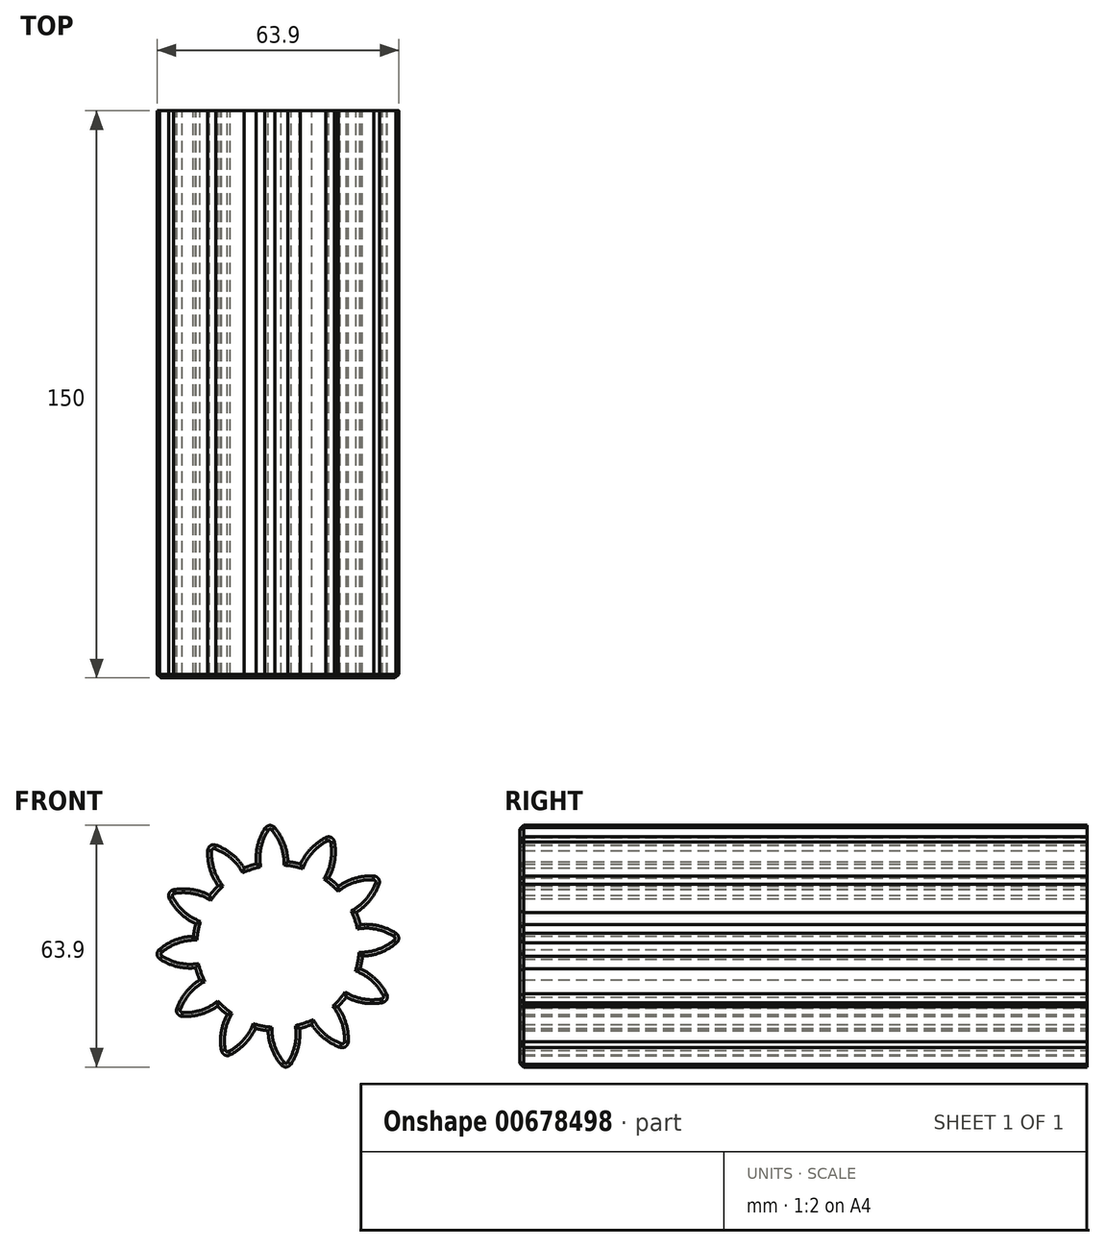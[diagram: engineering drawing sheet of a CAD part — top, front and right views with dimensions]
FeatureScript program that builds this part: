
annotation { "Feature Type Name" : "Feature", "Feature Type Description" : "" }
export const myFeature = defineFeature(function(context is Context, id is Id, definition is map)
    precondition{}
    {
        {
            var Q0;
            Q0=qCreatedBy(makeId("Front.planeOp"),FACE);
            var sketch = newSketch(context, id + "F0", { "sketchPlane" : qUnion([Q0])});
            skCircle(sketch, "E0", {"center": v(0, 0) * mm, "radius": 22.51 * mm});
            skCircle(sketch, "E1", {"center": v(0, 0) * mm, "radius": 27.14 * mm, "construction": true});
            skCircle(sketch, "E2", {"center": v(0, 0) * mm, "radius": 35.8 * mm, "construction": true});
            skLineSegment(sketch, "E3", {"start": v(0, 0) * mm, "end": v(0, 73.5) * mm, "construction": true});
            skLineSegment(sketch, "E4", {"start": v(0, 0) * mm, "end": v(-6.11, 73.5) * mm, "construction": true});
            skLineSegment(sketch, "E5", {"start": v(0, 27.14) * mm, "end": v(-50.23, 27.14) * mm, "construction": true});
            skLineSegment(sketch, "E6", {"start": v(0, 27.14) * mm, "end": v(-50.23, 8.86) * mm, "construction": true});
            skCircle(sketch, "E7", {"center": v(0, 0) * mm, "radius": 25.5 * mm, "construction": true});
            skCircle(sketch, "E8", {"center": v(0, 27.14) * mm, "radius": 14.6 * mm, "construction": true});
            skCircle(sketch, "E9", {"center": v(-13.72, 22.14) * mm, "radius": 14.6 * mm, "construction": true});
            skArc(sketch, "E10", {"start": v(0, 27.14) * mm, "mid": v(-2.78, 31.76) * mm, "end": v(-7.01, 35.11) * mm});
            skLineSegment(sketch, "E11", {"start": v(-0.11, -14.36) * mm, "end": v(0, -14.5) * mm});
            skLineSegment(sketch, "E12", {"start": v(0, -14.5) * mm, "end": v(0.11, -14.36) * mm});
            skLineSegment(sketch, "E13", {"start": v(0, 0) * mm, "end": v(-8.31, 126.81) * mm, "construction": true});
            skPoint(sketch, "E13.endSnap0", {"position": v(-8.31, 13.9) * mm});
            skArc(sketch, "E14", {"start": v(1.74, 26.9) * mm, "mid": v(0.63, 29.24) * mm, "end": v(-0.85, 31.36) * mm});
            skArc(sketch, "E15", {"start": v(2.61, 22.25) * mm, "mid": v(2.37, 24.61) * mm, "end": v(1.74, 26.9) * mm});
            skArc(sketch, "E16.MirrorCS", {"start": v(-5.43, 26.43) * mm, "mid": v(-4.64, 28.9) * mm, "end": v(-3.44, 31.19) * mm});
            skArc(sketch, "E17.MirrorCS", {"start": v(-5.7, 21.7) * mm, "mid": v(-5.76, 24.08) * mm, "end": v(-5.43, 26.43) * mm});
            skArc(sketch, "E18", {"start": v(-0.85, 31.36) * mm, "mid": v(-2.2, 31.95) * mm, "end": v(-3.44, 31.19) * mm});
            skSolve(sketch);
        }
        {
            var Q0;
            {var subQ0=sQuery(id+"F0.wireOp",EDGE,"E0");var subQ1=makeQuery(id+"F0.imprint","INTERSECT",VERTEX,{"derivedFrom":[subQ0,sQuery(id+"F0.wireOp",EDGE,"Z6IcxZwb-bq2U-V9Vx-4kxp-I47h1Pi9oaTY")]});Q0=makeQuery(id+"F0.imprint","IMPRINT",FACE,{"disambiguationData":[TD([[makeQuery(id+"F0.imprint","IMPRINT",EDGE,{"disambiguationData":[TD([[subQ1,-1.0]])],"derivedFrom":subQ0}),1.0]])]});}
            var Q1;
            Q1=makeQuery(id+"F0.imprint","IMPRINT",FACE,{"disambiguationData":[TD([[makeQuery(id+"F0.imprint","IMPRINT",EDGE,{"derivedFrom":sQuery(id+"F0.wireOp",EDGE,"E10")}),1.0]])]});
            var Q2;
            {var subQ2=sQuery(id+"F0.wireOp",EDGE,"E14");Q2=makeQuery(id+"F0.imprint","IMPRINT",FACE,{"disambiguationData":[TD([[makeQuery(id+"F0.imprint","IMPRINT",EDGE,{"derivedFrom":subQ2}),1.0]])]});}
            extrude(context, id + "F1", {"entities" : qUnion([Q0, Q1, Q2]), "depth" : 150 * mm, "offsetDistance" : 25 * mm});
        }
        {
            var Q0;
            Q0=makeQuery(id+"F1.opExtrude","CAP_EDGE",EDGE,{"disambiguationData":[OSD([sQuery(id+"F0.wireOp",EDGE,"E0")])],"isStart":false});
            var Q1;
            Q1=makeQuery(id+"F1.opExtrude","CAP_EDGE",EDGE,{"disambiguationData":[OSD([sQuery(id+"F0.wireOp",EDGE,"Z6IcxZwb-bq2U-V9Vx-4kxp-I47h1Pi9oaTY")])],"isStart":false});
            var Q2;
            Q2=makeQuery(id+"F1.opExtrude","CAP_EDGE",EDGE,{"disambiguationData":[OSD([sQuery(id+"F0.wireOp",EDGE,"820baf2d-91e2-4098-a2de-25aef56e50b20.MirrorCS")])],"isStart":false});
            var Q3;
            Q3=makeQuery(id+"F1.opExtrude","CAP_EDGE",EDGE,{"disambiguationData":[OSD([sQuery(id+"F0.wireOp",EDGE,"E10")])],"isStart":false});
            var Q4;
            Q4=makeQuery(id+"F1.opExtrude","CAP_EDGE",EDGE,{"disambiguationData":[OSD([sQuery(id+"F0.wireOp",EDGE,"af102f90-dcfa-482e-b3ce-9af33d462acd0.MirrorCS")])],"isStart":false});
            var Q5;
            Q5=makeQuery(id+"F1.opExtrude","CAP_EDGE",EDGE,{"disambiguationData":[OSD([sQuery(id+"F0.wireOp",EDGE,"u4poM2OA-MWgP-n9JE-3Qco-4fi2lhRNjPUH")])],"isStart":false});
            var Q6;
            Q6=makeQuery(id+"F1.opExtrude","CAP_EDGE",EDGE,{"disambiguationData":[OSD([sQuery(id+"F0.wireOp",EDGE,"E17.MirrorCS")])],"isStart":false});
            var Q7;
            Q7=makeQuery(id+"F1.opExtrude","CAP_EDGE",EDGE,{"disambiguationData":[OSD([sQuery(id+"F0.wireOp",EDGE,"E15")])],"isStart":false});
            var Q8;
            Q8=makeQuery(id+"F1.opExtrude","CAP_EDGE",EDGE,{"disambiguationData":[OSD([sQuery(id+"F0.wireOp",EDGE,"E18")])],"isStart":false});
            chamfer(context, id + "F2", {"entities" : qUnion([Q0, Q1, Q2, Q3, Q4, Q5, Q6, Q7, Q8]), "width" : 1 * mm, "tangentPropagation" : true});
        }
        {
            var Q0;
            Q0=makeQuery(id+"F1.opExtrude","SWEPT_BODY",BODY,{"disambiguationData":[OSD([sQuery(id+"F0.wireOp",EDGE,"E0"),sQuery(id+"F0.wireOp",EDGE,"E14"),sQuery(id+"F0.wireOp",EDGE,"E15"),sQuery(id+"F0.wireOp",EDGE,"E16.MirrorCS"),sQuery(id+"F0.wireOp",EDGE,"E17.MirrorCS"),sQuery(id+"F0.wireOp",EDGE,"E18")])]});
            var Q1;
            Q1=makeQuery(id+"F1.opExtrude","SWEPT_FACE",FACE,{"disambiguationData":[OSD([sQuery(id+"F0.wireOp",EDGE,"E0")])]});
            circularPattern(context, id + "F3", {"operationType" : NewBodyOperationType.ADD, "entities" : qUnion([Q0]), "axis" : qUnion([Q1]), "angle" : 360 * degree, "instanceCount" : 12, "equalSpace" : true});
        }
        {
            var Q0;
            Q0=makeQuery(id+"F1.opExtrude","SWEPT_BODY",BODY,{"disambiguationData":[OSD([sQuery(id+"F0.wireOp",EDGE,"E0"),sQuery(id+"F0.wireOp",EDGE,"E14"),sQuery(id+"F0.wireOp",EDGE,"E15"),sQuery(id+"F0.wireOp",EDGE,"E16.MirrorCS"),sQuery(id+"F0.wireOp",EDGE,"E17.MirrorCS"),sQuery(id+"F0.wireOp",EDGE,"E18")])]});
            transform(context, id + "F4", {"entities" : qUnion([Q0]), "transformType" : TransformType.TRANSLATION_3D, "dx" : 0 * mm, "dy" : 0 * mm, "dz" : 0 * mm, "makeCopy" : true});
        }
        {
            var Q0;
            Q0=makeQuery(id+"F4.opPattern","COPY",BODY,{"derivedFrom":makeQuery(id+"F1.opExtrude","SWEPT_BODY",BODY,{"disambiguationData":[OSD([sQuery(id+"F0.wireOp",EDGE,"E0"),sQuery(id+"F0.wireOp",EDGE,"E14"),sQuery(id+"F0.wireOp",EDGE,"E15"),sQuery(id+"F0.wireOp",EDGE,"E16.MirrorCS"),sQuery(id+"F0.wireOp",EDGE,"E17.MirrorCS"),sQuery(id+"F0.wireOp",EDGE,"E18")])]}),"instanceName":"1"});
            deleteBodies(context, id + "F5", {"entities" : qUnion([Q0])});
        }
    });
